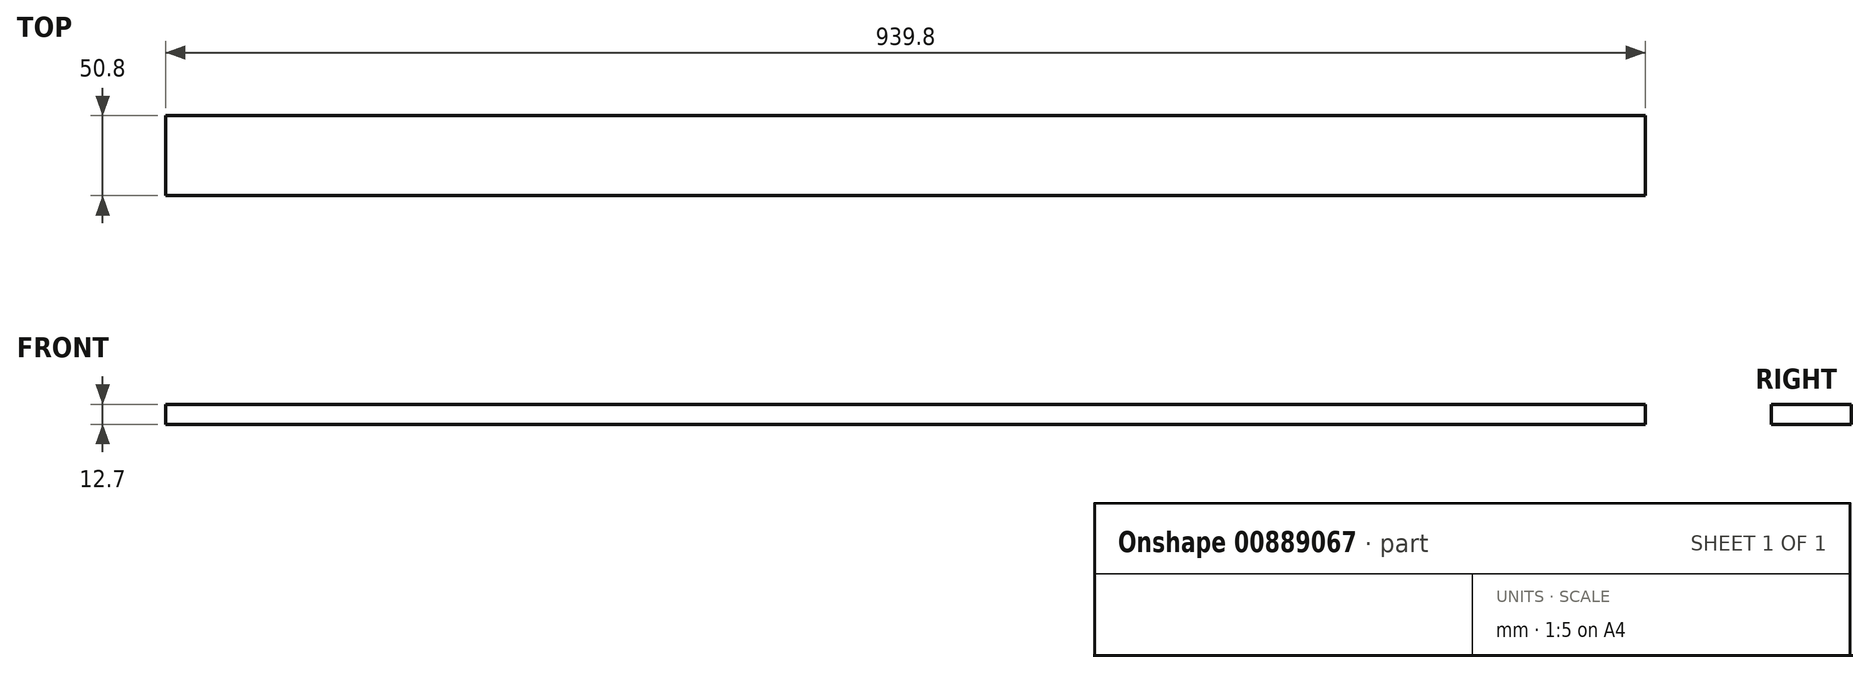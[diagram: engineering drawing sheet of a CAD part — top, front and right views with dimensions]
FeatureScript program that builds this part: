
annotation { "Feature Type Name" : "Feature", "Feature Type Description" : "" }
export const myFeature = defineFeature(function(context is Context, id is Id, definition is map)
    precondition{}
    {
        {
            var Q0;
            Q0=qCreatedBy(makeId("Top.planeOp"),FACE);
            var sketch = newSketch(context, id + "F0", { "sketchPlane" : qUnion([Q0])});
            skLineSegment(sketch, "E0.bottom", {"start": v(-469.9, 25.4) * mm, "end": v(469.9, 25.4) * mm});
            skLineSegment(sketch, "E0.top", {"start": v(-469.9, -25.4) * mm, "end": v(469.9, -25.4) * mm});
            skLineSegment(sketch, "E0.left", {"start": v(-469.9, 25.4) * mm, "end": v(-469.9, -25.4) * mm});
            skLineSegment(sketch, "E0.right", {"start": v(469.9, 25.4) * mm, "end": v(469.9, -25.4) * mm});
            skPoint(sketch, "E0.middle", {"position": v(0, 0) * mm});
            skSolve(sketch);
        }
        {
            var Q0;
            Q0 = qSketchRegion(id + "F0", true);
            extrude(context, id + "F1", {"entities" : qUnion([Q0]), "depth" : 12.7 * mm, "offsetDistance" : 25.4 * mm});
        }
    });
